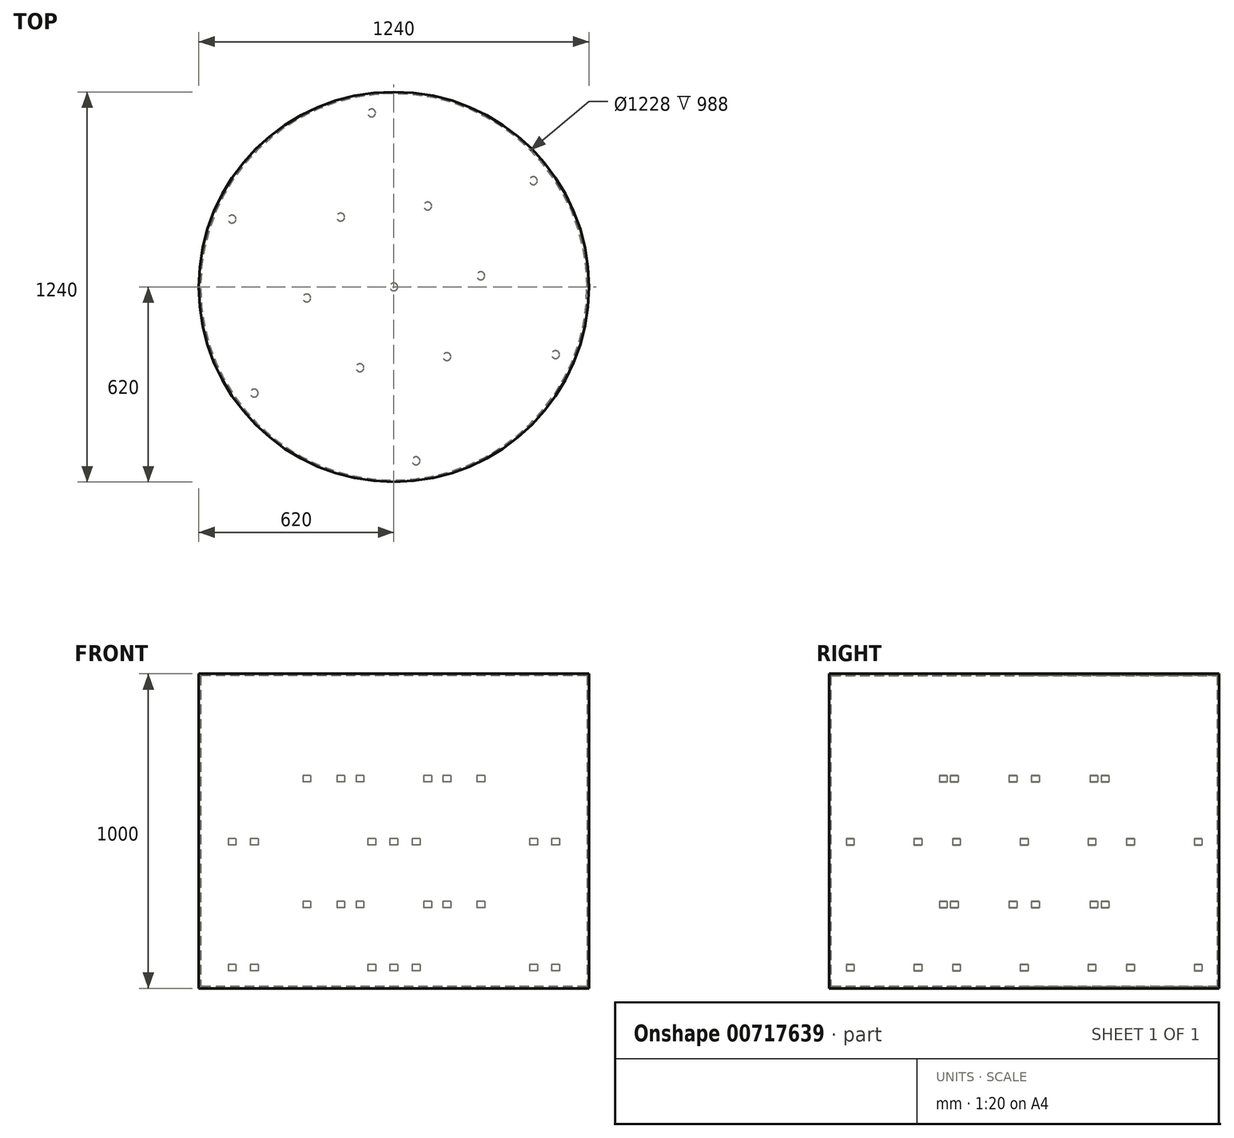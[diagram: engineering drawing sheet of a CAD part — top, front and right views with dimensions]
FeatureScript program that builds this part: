
annotation { "Feature Type Name" : "Feature", "Feature Type Description" : "" }
export const myFeature = defineFeature(function(context is Context, id is Id, definition is map)
    precondition{}
    {
        {
            var Q0;
            Q0=qCreatedBy(makeId("Top.planeOp"),FACE);
            var sketch = newSketch(context, id + "F0", { "sketchPlane" : qUnion([Q0])});
            skCircle(sketch, "E0", {"center": v(0, 0) * mm, "radius": 620 * mm});
            skSolve(sketch);
        }
        {
            var Q0;
            Q0=qSketchRegion(id+"F0",true);
            extrude(context, id + "F1", {"entities" : qUnion([Q0]), "depth" : 994 * mm, "offsetDistance" : 25 * mm});
        }
        {
            var Q0;
            Q0=makeQuery(id+"F1.opExtrude","CAP_FACE",FACE,{"disambiguationData":[OSD([sQuery(id+"F0.wireOp",EDGE,"E0")])],"isStart":false});
            shell(context, id + "F2", {"entities" : qUnion([Q0]), "thickness" : 6 * mm});
        }
        {
            var Q0;
            Q0=makeQuery(id+"F1.opExtrude","CAP_FACE",FACE,{"disambiguationData":[OSD([sQuery(id+"F0.wireOp",EDGE,"E0")])],"isStart":false});
            var sketch = newSketch(context, id + "F3", { "sketchPlane" : qUnion([Q0])});
            skCircle(sketch, "E1", {"center": v(0, 0) * mm, "radius": 620 * mm});
            skSolve(sketch);
        }
        {
            var Q0;
            Q0=qSketchRegion(id+"F3",true);
            extrude(context, id + "F4", {"entities" : qUnion([Q0]), "operationType" : NewBodyOperationType.ADD, "depth" : 6 * mm, "offsetDistance" : 25 * mm});
        }
        {
            var Q0;
            {var subQ0=sQuery(id+"F0.wireOp",EDGE,"E0");Q0=makeQuery(id+"F2.opShell","OFFSET_FACE",FACE,{"disambiguationData":[OSD([subQ0]),TDD([makeQuery(id+"F1.opExtrude","CAP_FACE",FACE,{"disambiguationData":[OSD([subQ0])],"isStart":true})])]});}
            cPlane(context, id + "F5", {"entities" : qUnion([Q0]), "cplaneType" : CPlaneType.OFFSET, "offset" : 50 * mm, "width" : 150 * mm, "height" : 150 * mm});
        }
        {
            var Q0;
            Q0=qCreatedBy(id+"F5.planeOp",FACE);
            var sketch = newSketch(context, id + "F6", { "sketchPlane" : qUnion([Q0])});
            skCircle(sketch, "E2", {"center": v(-443.66, -337.6) * mm, "radius": 12.5 * mm});
            skCircle(sketch, "E3.1.0", {"center": v(70.54, -553.02) * mm, "radius": 12.5 * mm});
            skCircle(sketch, "E3.2.0", {"center": v(514.2, -215.42) * mm, "radius": 12.5 * mm});
            skCircle(sketch, "E3.3.0", {"center": v(443.66, 337.6) * mm, "radius": 12.5 * mm});
            skCircle(sketch, "E3.4.0", {"center": v(-70.54, 553.02) * mm, "radius": 12.5 * mm});
            skCircle(sketch, "E3.5.0", {"center": v(-514.2, 215.42) * mm, "radius": 12.5 * mm});
            skPoint(sketch, "E3.center", {"position": v(0, 0) * mm});
            skCircle(sketch, "E4", {"center": v(0, 0) * mm, "radius": 12.5 * mm});
            skSolve(sketch);
        }
        {
            var Q0;
            Q0=qSketchRegion(id+"F6",true);
            extrude(context, id + "F7", {"entities" : qUnion([Q0]), "depth" : 20 * mm, "offsetDistance" : 25 * mm});
        }
        {
            var Q0;
            Q0=qCreatedBy(id+"F5.planeOp",FACE);
            cPlane(context, id + "F8", {"entities" : qUnion([Q0]), "cplaneType" : CPlaneType.OFFSET, "offset" : 200 * mm, "width" : 150 * mm, "height" : 150 * mm});
        }
        {
            var Q0;
            Q0=qCreatedBy(id+"F8.planeOp",FACE);
            var sketch = newSketch(context, id + "F9", { "sketchPlane" : qUnion([Q0])});
            skCircle(sketch, "E5", {"center": v(443.66, 337.6) * mm, "radius": 12.5 * mm});
            skLineSegment(sketch, "E6", {"start": v(0, 0) * mm, "end": v(-70.54, 553.02) * mm});
            skLineSegment(sketch, "E7", {"start": v(-70.54, 553.02) * mm, "end": v(443.66, 337.6) * mm});
            skLineSegment(sketch, "E8", {"start": v(443.66, 337.6) * mm, "end": v(0, 0) * mm});
            skCircle(sketch, "E9", {"center": v(-70.54, 553.02) * mm, "radius": 12.5 * mm});
            skLineSegment(sketch, "E10", {"start": v(0, 0) * mm, "end": v(102.88, 245.57) * mm});
            skCircle(sketch, "E11", {"center": v(107.7, 257.1) * mm, "radius": 12.5 * mm});
            skCircle(sketch, "E12.1.0", {"center": v(-168.8, 221.83) * mm, "radius": 12.5 * mm});
            skCircle(sketch, "E12.2.0", {"center": v(-276.5, -35.27) * mm, "radius": 12.5 * mm});
            skCircle(sketch, "E12.3.0", {"center": v(-107.7, -257.1) * mm, "radius": 12.5 * mm});
            skCircle(sketch, "E12.4.0", {"center": v(168.8, -221.83) * mm, "radius": 12.5 * mm});
            skCircle(sketch, "E12.5.0", {"center": v(276.5, 35.27) * mm, "radius": 12.5 * mm});
            skPoint(sketch, "E12.center", {"position": v(0, 0) * mm});
            skLineSegment(sketch, "E13.trimOffspring", {"start": v(112.54, 268.63) * mm, "end": v(186.56, 445.31) * mm});
            skSolve(sketch);
        }
        {
            var Q0;
            Q0=makeQuery(id+"F9.imprint","IMPRINT",FACE,{"disambiguationData":[TD([[makeQuery(id+"F9.imprint","IMPRINT",EDGE,{"derivedFrom":sQuery(id+"F9.wireOp",EDGE,"E12.1.0")}),1.0]])]});
            var Q1;
            Q1=makeQuery(id+"F9.imprint","IMPRINT",FACE,{"disambiguationData":[TD([[makeQuery(id+"F9.imprint","IMPRINT",EDGE,{"derivedFrom":sQuery(id+"F9.wireOp",EDGE,"E12.2.0")}),1.0]])]});
            var Q2;
            Q2=makeQuery(id+"F9.imprint","IMPRINT",FACE,{"disambiguationData":[TD([[makeQuery(id+"F9.imprint","IMPRINT",EDGE,{"derivedFrom":sQuery(id+"F9.wireOp",EDGE,"E12.3.0")}),1.0]])]});
            var Q3;
            Q3=makeQuery(id+"F9.imprint","IMPRINT",FACE,{"disambiguationData":[TD([[makeQuery(id+"F9.imprint","IMPRINT",EDGE,{"derivedFrom":sQuery(id+"F9.wireOp",EDGE,"E12.4.0")}),1.0]])]});
            var Q4;
            Q4=makeQuery(id+"F9.imprint","IMPRINT",FACE,{"disambiguationData":[TD([[makeQuery(id+"F9.imprint","IMPRINT",EDGE,{"derivedFrom":sQuery(id+"F9.wireOp",EDGE,"E12.5.0")}),1.0]])]});
            var Q5;
            {var subQ0=sQuery(id+"F9.wireOp",EDGE,"E11");var subQ1=makeQuery(id+"F9.imprint","INTERSECT",VERTEX,{"derivedFrom":[sQuery(id+"F9.wireOp",EDGE,"E10"),subQ0]});Q5=makeQuery(id+"F9.imprint","IMPRINT",FACE,{"disambiguationData":[TD([[makeQuery(id+"F9.imprint","IMPRINT",EDGE,{"disambiguationData":[TD([[subQ1,1.0]])],"derivedFrom":subQ0}),1.0]])]});}
            extrude(context, id + "F10", {"entities" : qUnion([Q0, Q1, Q2, Q3, Q4, Q5]), "depth" : 20 * mm, "offsetDistance" : 25 * mm});
        }
        {
            var Q0;
            Q0=qCreatedBy(id+"F8.planeOp",FACE);
            cPlane(context, id + "F11", {"entities" : qUnion([Q0]), "cplaneType" : CPlaneType.OFFSET, "offset" : 200 * mm, "width" : 150 * mm, "height" : 150 * mm});
        }
        {
            var Q0;
            Q0=qCreatedBy(id+"F11.planeOp",FACE);
            var sketch = newSketch(context, id + "F12", { "sketchPlane" : qUnion([Q0])});
            skCircle(sketch, "E14", {"center": v(-443.66, -337.6) * mm, "radius": 12.5 * mm});
            skCircle(sketch, "E15.1.0", {"center": v(70.54, -553.02) * mm, "radius": 12.5 * mm});
            skCircle(sketch, "E15.2.0", {"center": v(514.2, -215.42) * mm, "radius": 12.5 * mm});
            skCircle(sketch, "E15.3.0", {"center": v(443.66, 337.6) * mm, "radius": 12.5 * mm});
            skCircle(sketch, "E15.4.0", {"center": v(-70.54, 553.02) * mm, "radius": 12.5 * mm});
            skCircle(sketch, "E15.5.0", {"center": v(-514.2, 215.42) * mm, "radius": 12.5 * mm});
            skPoint(sketch, "E15.center", {"position": v(0, 0) * mm});
            skCircle(sketch, "E16", {"center": v(0, 0) * mm, "radius": 12.5 * mm});
            skSolve(sketch);
        }
        {
            var Q0;
            Q0=qSketchRegion(id+"F12",true);
            extrude(context, id + "F13", {"entities" : qUnion([Q0]), "depth" : 20 * mm, "offsetDistance" : 25 * mm});
        }
        {
            var Q0;
            Q0=qCreatedBy(id+"F11.planeOp",FACE);
            cPlane(context, id + "F14", {"entities" : qUnion([Q0]), "cplaneType" : CPlaneType.OFFSET, "offset" : 200 * mm, "width" : 150 * mm, "height" : 150 * mm});
        }
        {
            var Q0;
            Q0=qCreatedBy(id+"F14.planeOp",FACE);
            var sketch = newSketch(context, id + "F15", { "sketchPlane" : qUnion([Q0])});
            skCircle(sketch, "E17", {"center": v(443.66, 337.6) * mm, "radius": 12.5 * mm});
            skLineSegment(sketch, "E18", {"start": v(0, 0) * mm, "end": v(-70.54, 553.02) * mm});
            skLineSegment(sketch, "E19", {"start": v(-70.54, 553.02) * mm, "end": v(443.66, 337.6) * mm});
            skLineSegment(sketch, "E20", {"start": v(443.66, 337.6) * mm, "end": v(0, 0) * mm});
            skCircle(sketch, "E21", {"center": v(-70.54, 553.02) * mm, "radius": 12.5 * mm});
            skLineSegment(sketch, "E22", {"start": v(0, 0) * mm, "end": v(102.88, 245.57) * mm});
            skCircle(sketch, "E23", {"center": v(107.7, 257.1) * mm, "radius": 12.5 * mm});
            skCircle(sketch, "E24.1.0", {"center": v(-168.8, 221.83) * mm, "radius": 12.5 * mm});
            skCircle(sketch, "E24.2.0", {"center": v(-276.5, -35.27) * mm, "radius": 12.5 * mm});
            skCircle(sketch, "E24.3.0", {"center": v(-107.7, -257.1) * mm, "radius": 12.5 * mm});
            skCircle(sketch, "E24.4.0", {"center": v(168.8, -221.83) * mm, "radius": 12.5 * mm});
            skCircle(sketch, "E24.5.0", {"center": v(276.5, 35.27) * mm, "radius": 12.5 * mm});
            skPoint(sketch, "E24.center", {"position": v(0, 0) * mm});
            skLineSegment(sketch, "E25.trimOffspring", {"start": v(112.54, 268.63) * mm, "end": v(186.56, 445.31) * mm});
            skSolve(sketch);
        }
        {
            var Q0;
            Q0=makeQuery(id+"F15.imprint","IMPRINT",FACE,{"disambiguationData":[TD([[makeQuery(id+"F15.imprint","IMPRINT",EDGE,{"derivedFrom":sQuery(id+"F15.wireOp",EDGE,"E24.1.0")}),1.0]])]});
            var Q1;
            {var subQ0=sQuery(id+"F15.wireOp",EDGE,"E23");var subQ1=makeQuery(id+"F15.imprint","INTERSECT",VERTEX,{"derivedFrom":[sQuery(id+"F15.wireOp",EDGE,"E22"),subQ0]});Q1=makeQuery(id+"F15.imprint","IMPRINT",FACE,{"disambiguationData":[TD([[makeQuery(id+"F15.imprint","IMPRINT",EDGE,{"disambiguationData":[TD([[subQ1,1.0]])],"derivedFrom":subQ0}),1.0]])]});}
            var Q2;
            Q2=makeQuery(id+"F15.imprint","IMPRINT",FACE,{"disambiguationData":[TD([[makeQuery(id+"F15.imprint","IMPRINT",EDGE,{"derivedFrom":sQuery(id+"F15.wireOp",EDGE,"E24.5.0")}),1.0]])]});
            var Q3;
            Q3=makeQuery(id+"F15.imprint","IMPRINT",FACE,{"disambiguationData":[TD([[makeQuery(id+"F15.imprint","IMPRINT",EDGE,{"derivedFrom":sQuery(id+"F15.wireOp",EDGE,"E24.4.0")}),1.0]])]});
            var Q4;
            Q4=makeQuery(id+"F15.imprint","IMPRINT",FACE,{"disambiguationData":[TD([[makeQuery(id+"F15.imprint","IMPRINT",EDGE,{"derivedFrom":sQuery(id+"F15.wireOp",EDGE,"E24.3.0")}),1.0]])]});
            var Q5;
            Q5=makeQuery(id+"F15.imprint","IMPRINT",FACE,{"disambiguationData":[TD([[makeQuery(id+"F15.imprint","IMPRINT",EDGE,{"derivedFrom":sQuery(id+"F15.wireOp",EDGE,"E24.2.0")}),1.0]])]});
            extrude(context, id + "F16", {"entities" : qUnion([Q0, Q1, Q2, Q3, Q4, Q5]), "depth" : 20 * mm, "offsetDistance" : 25 * mm});
        }
    });
